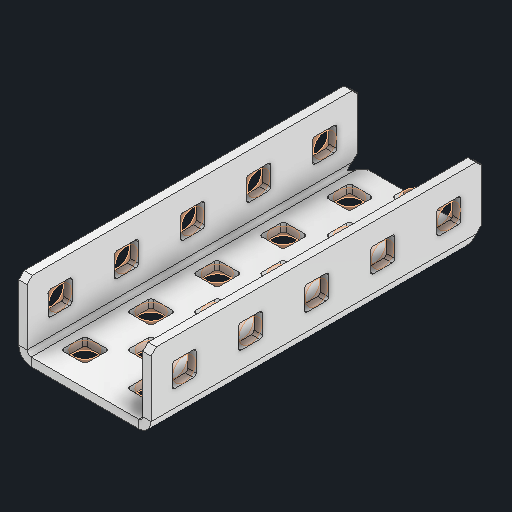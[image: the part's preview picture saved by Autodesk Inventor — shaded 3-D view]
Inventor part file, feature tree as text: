
AUTODESK INVENTOR PART (.ipt)
format: ipt  version: 2024 (Build 280153000, 153)  size: 579,584 bytes
history: native  units: in
note: dims shown in document units (in); Inventor stores cm internally (conversion verified against a paired STEP export)
features: other x32, extrude x23, sheet_metal_op x11, pattern_linear x2, mirror x1, chamfer x1, sketch x1
ambient origin geometry x8: Origin, YZ Plane, XZ Plane, XY Plane, X Axis, Y Axis, Z Axis, Center Point
bodies: Solid1 (feature_tree), Body (feature_tree)
feature tree (71):
  sheet_metal_op  "Flanges"
  other  "Flange Pattern Plane"
  other  "Flange Pattern Sketch"
  sheet_metal_op  "Flange Pattern"
  sheet_metal_op  "Body Pattern"
  pattern_linear  "Center Pattern"  Spacing1=2.5in  [1 undecoded]
  other  "Arc Length"
  mirror  "Notch Mirror"
  pattern_linear  "Notch Pattern"  Spacing1=0.0625in  [1 undecoded]
  chamfer  "End Chamfer"
  extrude  "Half Cut"  Depth=0.0625in
  other  "Plate1"
  sketch  "Sketch2"  dims[d0=1.0in d1=2.5in d2=0.0625in d3=0.0625in d4=0.0312in d5=0.125in d6=0.0625in d7=0.5in d8=90.0deg d9=0.0312in d10=0.25in d11=0.0625in d12=0.0625in d16=0.182in d17=0.02in d18=0.0625in d19=0.0in d20=0.25in d21=0.25in d38=1.9685in d40=0.5in d41=0.7874in d43=1.0in d46=0.172in d47=1.0in d48=0.0in d49=0.182in d50=0.02in d51=0.25in d52=0.25in d53=0.0625in d54=0.0in d55=0.172in d56=1.0in d57=0.0in d58=0.25in d60=1.9685in d62=0.5in d63=0.7874in d65=0.5in d85=0.1473in d86=0.1782in d88=0.04in d89=0.0625in d90=0.0in d91=0.04in d92=0.0491in d95=2.5in d96=0.04in d97=0.25in d98=45.0deg d99=0.25in d100=0.5in d101=0.0in d102=2.497in d106=0.182in d107=0.02in d108=0.5in d109=0.5in d110=0.0625in d111=0.0in d112=0.172in d113=0.5in d114=0.0in d117=0.5in d118=0.5in d119=0.5in]
  other  "Plate2"
  sheet_metal_op  "Bend1"
  sheet_metal_op  "Corner1"
  other  "Srf1"
  other  "Srf2"
  other  "Srf91"
  sheet_metal_op  "Body Pattern Sketch"
  other  "Srf92"
  other  "Srf786"
  other  "Srf823"
  other  "Srf824"
  other  "Srf825"
  other  "Srf826"
  other  "Srf827"
  other  "Srf828"
  other  "Srf829"
  other  "Srf856"
  other  "Srf857"
  other  "Srf858"
  other  "Srf859"
  other  "Srf860"
  other  "Srf861"
  other  "Srf862"
  other  "Srf889"
  other  "Srf890"
  other  "Srf891"
  other  "Srf892"
  other  "Srf922"
  other  "Srf959"
  sheet_metal_op  "Flange Stamp"
  sheet_metal_op  "Flange Circle"
  sheet_metal_op  "Body Stamp"
  sheet_metal_op  "Body Circle"
  other  "Center Stamp"
  other  "Center Circle"
  sheet_metal_op  "Notch"
  extrude  "ExtrusionSrf2"  Depth=0.0312in
  extrude  "ExtrusionSrf92"  Depth=0.5in
  extrude  "ExtrusionSrf823"  Depth=0.0625in
  extrude  "ExtrusionSrf824"  Depth=0.5in TaperAngle=90.0deg
  extrude  "ExtrusionSrf825"  Depth=0.5in
  extrude  "ExtrusionSrf826"  Depth=0.0625in
  extrude  "ExtrusionSrf827"  Depth=0.0625in
  extrude  "ExtrusionSrf828"  Depth=0.5in
  extrude  "ExtrusionSrf829"  Depth=0.02in
  extrude  "ExtrusionSrf856"  Depth=0.0625in
  extrude  "ExtrusionSrf857"  TaperAngle=0.0deg  [1 undecoded]
  extrude  "ExtrusionSrf858"  Depth=0.5in
  extrude  "ExtrusionSrf859"  Depth=0.5in
  extrude  "ExtrusionSrf860"  Depth=0.5in
  extrude  "ExtrusionSrf861"  Depth=0.5in
  extrude  "ExtrusionSrf862"  Depth=1.0in TaperAngle=0.0deg
  extrude  "ExtrusionSrf889"  Depth=0.5in
  extrude  "ExtrusionSrf890"  Depth=0.02in
  extrude  "ExtrusionSrf891"  Depth=0.5in
  extrude  "ExtrusionSrf892"  Depth=0.5in
  extrude  "ExtrusionSrf922"  Depth=0.0625in
  extrude  "ExtrusionSrf959"  TaperAngle=0.0deg  [1 undecoded]
note: 4 required parameter values undecoded (feature->parameter linkage not recoverable at this tier; creation-order binding heuristic only, values carry confidence <= 0.55)
